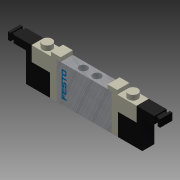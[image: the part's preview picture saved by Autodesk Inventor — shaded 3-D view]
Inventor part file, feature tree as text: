
AUTODESK INVENTOR PART (.ipt)
format: ipt  version: 2011 (Build 150239000, 239)  size: 3,063,296 bytes
history: native  units: in
note: dims shown in document units (in); Inventor stores cm internally (conversion verified against a paired STEP export)
features: sketch x12, extrude x11, projected_geometry x9, other x2, plane x1
ambient origin geometry x8: Origin, YZ Plane, XZ Plane, XY Plane, X Axis, Y Axis, Z Axis, Center Point
bodies: Solid1 (feature_tree)
feature tree (35):
  extrude  "Extrusion1"  Depth=3.6in
  extrude  "Extrusion2"  Depth=0.3in
  extrude  "Extrusion3"  Depth=0.125in
  extrude  "Extrusion4"  Depth=0.125in
  extrude  "Extrusion5"  Depth=0.775in
  extrude  "Extrusion6"  Depth=0.375in TaperAngle=0.0deg
  plane  "Work Plane1"
  extrude  "Extrusion7"  Depth=0.125in
  extrude  "Extrusion8"  Depth=0.2in
  extrude  "Extrusion9"  Depth=0.775in
  extrude  "Extrusion10"  Depth=0.45in
  extrude  "Extrusion11"  Depth=0.001in TaperAngle=0.0deg
  other  "Decal1"
  sketch  "Sketch1"  dims[d0=1.125in d1=3.6in]
  sketch  "Sketch2"  dims[d2=0.3in d3=0.3in]
  sketch  "Sketch3"  dims[d4=0.125in d5=0.125in]
  sketch  "Sketch4"  dims[d6=0.125in d7=0.125in]
  projected_geometry  "Projected Loop1"
  sketch  "Sketch5"  dims[d8=0.775in d9=0.775in]
  projected_geometry  "Projected Loop2"
  projected_geometry  "Projected Loop3"
  sketch  "Sketch6"  dims[d10=1.45in d11=0.375in d12=0.0in]
  projected_geometry  "Projected Loop4"
  sketch  "Sketch7"  dims[d13=0.125in d14=0.125in]
  projected_geometry  "Projected Loop5"
  projected_geometry  "Projected Loop6"
  sketch  "Sketch8"  dims[d15=0.2in d16=0.2in]
  projected_geometry  "Projected Loop7"
  projected_geometry  "Projected Loop8"
  sketch  "Sketch9"  dims[d17=0.775in d18=0.775in]
  projected_geometry  "Projected Loop9"
  sketch  "Sketch10"  dims[d19=0.45in d20=0.45in]
  sketch  "Sketch11"  dims[d21=0.001in d22=0.0in d23=0.001in d24=0.0in]
  sketch  "Sketch12"  dims[d25=0.001in d26=0.0in d27=0.001in d28=0.0in d29=0.375in d30=0.375in d31=0.225in d32=0.225in d33=0.375in d34=0.0in d35=0.1875in d36=0.1in d37=0.1in d38=0.15in d39=0.15in d40=0.0375in d41=0.0375in d42=0.0375in d43=0.25in d44=0.0in d45=0.0in d46=0.0in d47=0.0in d48=0.0in d49=0.075in d50=0.225in d51=0.0in d52=0.075in d53=0.0in d54=0.375in d55=0.0in d56=0.3in d57=0.3in d58=0.15in d59=0.0in d60=0.25in d61=0.425in d62=0.425in d63=0.425in d64=0.425in d65=0.4in d66=0.0in d67=0.25in d68=0.425in d69=0.4in d70=0.0in d72=0.8in d84=0.15in d85=0.1625in d86=0.1625in]
  other  "Image1"
